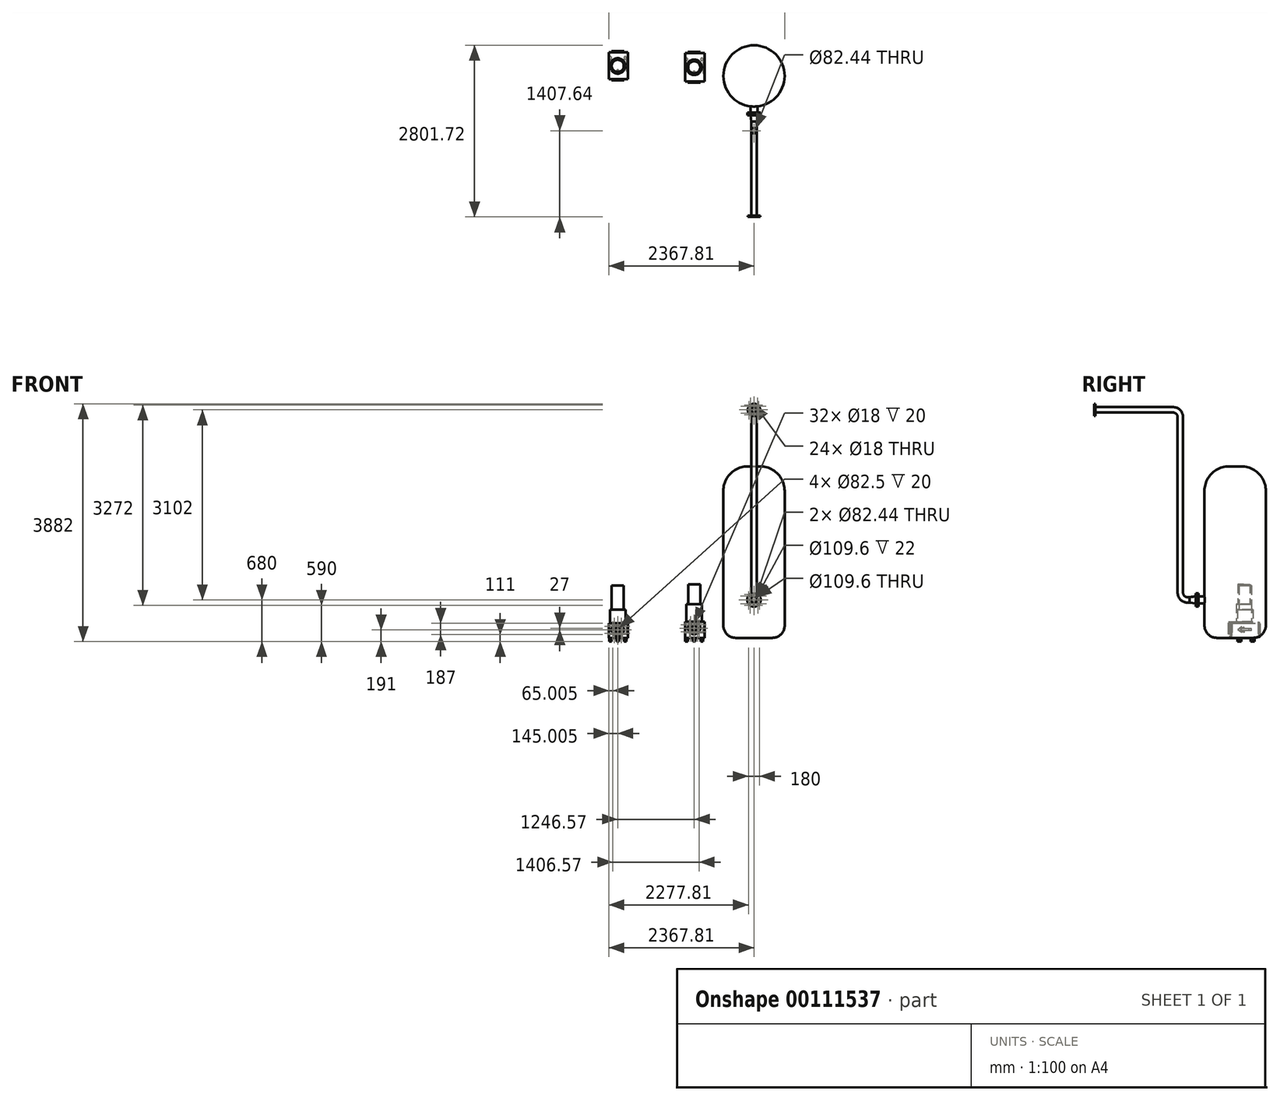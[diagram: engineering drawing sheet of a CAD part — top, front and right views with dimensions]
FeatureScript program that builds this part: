
annotation { "Feature Type Name" : "Feature", "Feature Type Description" : "" }
export const myFeature = defineFeature(function(context is Context, id is Id, definition is map)
    precondition{}
    {
        {
            var Q0;
            Q0=qCreatedBy(makeId("Top.planeOp"),FACE);
            var sketch = newSketch(context, id + "F0", { "sketchPlane" : qUnion([Q0])});
            skLineSegment(sketch, "E0.bottom", {"start": v(-836.3, 113.91) * mm, "end": v(-523.3, 113.91) * mm});
            skLineSegment(sketch, "E0.top", {"start": v(-836.3, -361.09) * mm, "end": v(-523.3, -361.09) * mm});
            skLineSegment(sketch, "E0.left", {"start": v(-836.3, 113.91) * mm, "end": v(-836.3, -361.09) * mm});
            skLineSegment(sketch, "E0.right", {"start": v(-523.3, 113.91) * mm, "end": v(-523.3, -361.09) * mm});
            skLineSegment(sketch, "E1.bottom", {"start": v(405.26, 101.65) * mm, "end": v(725.26, 101.65) * mm});
            skLineSegment(sketch, "E1.top", {"start": v(405.26, -398.35) * mm, "end": v(725.26, -398.35) * mm});
            skLineSegment(sketch, "E1.left", {"start": v(405.26, 101.65) * mm, "end": v(405.26, -398.35) * mm});
            skLineSegment(sketch, "E1.right", {"start": v(725.26, 101.65) * mm, "end": v(725.26, -398.35) * mm});
            skSolve(sketch);
        }
        {
            var Q0;
            Q0=makeQuery(id+"F0.imprint","IMPRINT",FACE,{"disambiguationData":[TD([[makeQuery(id+"F0.imprint","IMPRINT",EDGE,{"derivedFrom":sQuery(id+"F0.wireOp",EDGE,"E0.bottom")}),-1.0]])]});
            extrude(context, id + "F1", {"entities" : qUnion([Q0]), "depth" : 853 * mm});
        }
        {
            var Q0;
            Q0=makeQuery(id+"F1.opExtrude","SWEPT_FACE",FACE,{"disambiguationData":[OSD([sQuery(id+"F0.wireOp",EDGE,"E0.right")])]});
            cPlane(context, id + "F2", {"entities" : qUnion([Q0]), "cplaneType" : CPlaneType.OFFSET, "offset" : 168 * mm, "oppositeDirection" : true, "width" : 150 * mm, "height" : 150 * mm});
        }
        {
            var Q0;
            Q0=qCreatedBy(id+"F2.planeOp",FACE);
            var sketch = newSketch(context, id + "F3", { "sketchPlane" : qUnion([Q0])});
            skPoint(sketch, "E2", {"position": v(113.91, 426.5) * mm});
            skLineSegment(sketch, "E3", {"start": v(-27.09, 853) * mm, "end": v(-27.09, 463) * mm});
            skLineSegment(sketch, "E4", {"start": v(-27.09, 463) * mm, "end": v(-1.09, 463) * mm});
            skLineSegment(sketch, "E5", {"start": v(-1.09, 463) * mm, "end": v(-1.09, 236.83) * mm});
            skLineSegment(sketch, "E6", {"start": v(-1.09, 236.83) * mm, "end": v(113.91, 236.83) * mm});
            skLineSegment(sketch, "E7", {"start": v(-126.09, 872.7) * mm, "end": v(-126.09, -37.26) * mm, "construction": true});
            skLineSegment(sketch, "E8", {"start": v(-496.13, 131) * mm, "end": v(240.4, 131) * mm, "construction": true});
            skLineSegment(sketch, "E9", {"start": v(-27.09, 853) * mm, "end": v(558.03, 853) * mm});
            skLineSegment(sketch, "E10", {"start": v(558.03, 853) * mm, "end": v(558.03, 236.83) * mm});
            skLineSegment(sketch, "E11", {"start": v(558.03, 236.83) * mm, "end": v(113.91, 236.83) * mm});
            skSolve(sketch);
        }
        {
            var Q0;
            {var subQ2=sQuery(id+"F3.wireOp",EDGE,"E3");Q0=makeQuery(id+"F3.imprint","IMPRINT",FACE,{"disambiguationData":[TD([[makeQuery(id+"F3.imprint","IMPRINT",EDGE,{"derivedFrom":subQ2}),1.0]])]});}
            var Q1;
            Q1=sQuery(id+"F3.wireOp",EDGE,"E7");
            revolve(context, id + "F4", {"operationType" : NewBodyOperationType.REMOVE, "entities" : qUnion([Q0]), "axis" : qUnion([Q1]), "revolveType" : RevolveType.FULL, "oppositeDirection" : true});
        }
        {
            var Q0;
            Q0=makeQuery(id+"F1.opExtrude","SWEPT_FACE",FACE,{"disambiguationData":[OSD([sQuery(id+"F0.wireOp",EDGE,"E0.top")])]});
            var sketch = newSketch(context, id + "F5", { "sketchPlane" : qUnion([Q0])});
            skPoint(sketch, "E12.0", {"position": v(-691.3, 131) * mm});
            skCircle(sketch, "E13.2.0", {"center": v(-611.3, 131) * mm, "radius": 9 * mm});
            skCircle(sketch, "E13.1.0", {"center": v(-634.74, 74.43) * mm, "radius": 9 * mm});
            skCircle(sketch, "E14", {"center": v(-691.3, 131) * mm, "radius": 100 * mm});
            skCircle(sketch, "E13.3.0", {"center": v(-634.74, 187.57) * mm, "radius": 9 * mm});
            skCircle(sketch, "E15", {"center": v(-691.3, 51) * mm, "radius": 9 * mm});
            skCircle(sketch, "E16", {"center": v(-691.3, 131) * mm, "radius": 80 * mm, "construction": true});
            skCircle(sketch, "E17", {"center": v(-691.3, 131) * mm, "radius": 45.25 * mm});
            skCircle(sketch, "E13.6.0", {"center": v(-771.3, 131) * mm, "radius": 9 * mm});
            skCircle(sketch, "E18", {"center": v(-691.3, 131) * mm, "radius": 44.45 * mm});
            skCircle(sketch, "E13.4.0", {"center": v(-691.3, 211) * mm, "radius": 9 * mm});
            skCircle(sketch, "E13.7.0", {"center": v(-747.87, 74.43) * mm, "radius": 9 * mm});
            skCircle(sketch, "E13.5.0", {"center": v(-747.87, 187.57) * mm, "radius": 9 * mm});
            skCircle(sketch, "E19.0", {"center": v(-691.3, 131) * mm, "radius": 41.25 * mm});
            skSolve(sketch);
        }
        {
            var Q0;
            Q0=makeQuery(id+"F5.imprint","IMPRINT",FACE,{"disambiguationData":[TD([[makeQuery(id+"F5.imprint","IMPRINT",EDGE,{"derivedFrom":sQuery(id+"F5.wireOp",EDGE,"E14")}),-1.0]])]});
            var Q1;
            Q1=makeQuery(id+"F5.imprint","IMPRINT",FACE,{"disambiguationData":[TD([[makeQuery(id+"F5.imprint","IMPRINT",EDGE,{"derivedFrom":sQuery(id+"F5.wireOp",EDGE,"E13.5.0")}),1.0]])]});
            var Q2;
            Q2=makeQuery(id+"F5.imprint","IMPRINT",FACE,{"disambiguationData":[TD([[makeQuery(id+"F5.imprint","IMPRINT",EDGE,{"derivedFrom":sQuery(id+"F5.wireOp",EDGE,"E13.4.0")}),1.0]])]});
            var Q3;
            Q3=makeQuery(id+"F5.imprint","IMPRINT",FACE,{"disambiguationData":[TD([[makeQuery(id+"F5.imprint","IMPRINT",EDGE,{"derivedFrom":sQuery(id+"F5.wireOp",EDGE,"E13.3.0")}),1.0]])]});
            var Q4;
            Q4=makeQuery(id+"F5.imprint","IMPRINT",FACE,{"disambiguationData":[TD([[makeQuery(id+"F5.imprint","IMPRINT",EDGE,{"derivedFrom":sQuery(id+"F5.wireOp",EDGE,"E13.2.0")}),1.0]])]});
            var Q5;
            Q5=makeQuery(id+"F5.imprint","IMPRINT",FACE,{"disambiguationData":[TD([[makeQuery(id+"F5.imprint","IMPRINT",EDGE,{"derivedFrom":sQuery(id+"F5.wireOp",EDGE,"E13.1.0")}),1.0]])]});
            var Q6;
            Q6=makeQuery(id+"F5.imprint","IMPRINT",FACE,{"disambiguationData":[TD([[makeQuery(id+"F5.imprint","IMPRINT",EDGE,{"derivedFrom":sQuery(id+"F5.wireOp",EDGE,"E15")}),1.0]])]});
            var Q7;
            Q7=makeQuery(id+"F5.imprint","IMPRINT",FACE,{"disambiguationData":[TD([[makeQuery(id+"F5.imprint","IMPRINT",EDGE,{"derivedFrom":sQuery(id+"F5.wireOp",EDGE,"E13.7.0")}),1.0]])]});
            var Q8;
            Q8=makeQuery(id+"F5.imprint","IMPRINT",FACE,{"disambiguationData":[TD([[makeQuery(id+"F5.imprint","IMPRINT",EDGE,{"derivedFrom":sQuery(id+"F5.wireOp",EDGE,"E13.6.0")}),1.0]])]});
            var Q9;
            Q9=makeQuery(id+"F5.imprint","IMPRINT",FACE,{"disambiguationData":[TD([[makeQuery(id+"F5.imprint","IMPRINT",EDGE,{"derivedFrom":sQuery(id+"F5.wireOp",EDGE,"E19.0")}),1.0]])]});
            extrude(context, id + "F6", {"entities" : qUnion([Q0, Q1, Q2, Q3, Q4, Q5, Q6, Q7, Q8, Q9]), "operationType" : NewBodyOperationType.REMOVE, "oppositeDirection" : true, "depth" : 20 * mm});
        }
        {
            var Q0;
            Q0=makeQuery(id+"F1.opExtrude","SWEPT_FACE",FACE,{"disambiguationData":[OSD([sQuery(id+"F0.wireOp",EDGE,"E0.bottom")])]});
            var sketch = newSketch(context, id + "F7", { "sketchPlane" : qUnion([Q0])});
            skPoint(sketch, "E20.0", {"position": v(691.3, 131) * mm});
            skCircle(sketch, "E21.2.0", {"center": v(771.3, 131) * mm, "radius": 9 * mm});
            skCircle(sketch, "E21.1.0", {"center": v(747.87, 74.43) * mm, "radius": 9 * mm});
            skCircle(sketch, "E22", {"center": v(691.3, 131) * mm, "radius": 100 * mm});
            skCircle(sketch, "E21.3.0", {"center": v(747.87, 187.57) * mm, "radius": 9 * mm});
            skCircle(sketch, "E23", {"center": v(691.3, 51) * mm, "radius": 9 * mm});
            skCircle(sketch, "E24", {"center": v(691.3, 131) * mm, "radius": 80 * mm, "construction": true});
            skCircle(sketch, "E25", {"center": v(691.3, 131) * mm, "radius": 45.25 * mm});
            skCircle(sketch, "E21.6.0", {"center": v(611.3, 131) * mm, "radius": 9 * mm});
            skCircle(sketch, "E26", {"center": v(691.3, 131) * mm, "radius": 44.45 * mm});
            skCircle(sketch, "E21.4.0", {"center": v(691.3, 211) * mm, "radius": 9 * mm});
            skCircle(sketch, "E21.7.0", {"center": v(634.74, 74.43) * mm, "radius": 9 * mm});
            skCircle(sketch, "E21.5.0", {"center": v(634.74, 187.57) * mm, "radius": 9 * mm});
            skCircle(sketch, "E27.0", {"center": v(691.3, 131) * mm, "radius": 41.25 * mm});
            skSolve(sketch);
        }
        {
            var Q0;
            Q0=makeQuery(id+"F7.imprint","IMPRINT",FACE,{"disambiguationData":[TD([[makeQuery(id+"F7.imprint","IMPRINT",EDGE,{"derivedFrom":sQuery(id+"F7.wireOp",EDGE,"E22")}),-1.0]])]});
            var Q1;
            Q1=makeQuery(id+"F7.imprint","IMPRINT",FACE,{"disambiguationData":[TD([[makeQuery(id+"F7.imprint","IMPRINT",EDGE,{"derivedFrom":sQuery(id+"F7.wireOp",EDGE,"E21.4.0")}),1.0]])]});
            var Q2;
            Q2=makeQuery(id+"F7.imprint","IMPRINT",FACE,{"disambiguationData":[TD([[makeQuery(id+"F7.imprint","IMPRINT",EDGE,{"derivedFrom":sQuery(id+"F7.wireOp",EDGE,"E21.3.0")}),1.0]])]});
            var Q3;
            Q3=makeQuery(id+"F7.imprint","IMPRINT",FACE,{"disambiguationData":[TD([[makeQuery(id+"F7.imprint","IMPRINT",EDGE,{"derivedFrom":sQuery(id+"F7.wireOp",EDGE,"E21.5.0")}),1.0]])]});
            var Q4;
            Q4=makeQuery(id+"F7.imprint","IMPRINT",FACE,{"disambiguationData":[TD([[makeQuery(id+"F7.imprint","IMPRINT",EDGE,{"derivedFrom":sQuery(id+"F7.wireOp",EDGE,"E21.6.0")}),1.0]])]});
            var Q5;
            Q5=makeQuery(id+"F7.imprint","IMPRINT",FACE,{"disambiguationData":[TD([[makeQuery(id+"F7.imprint","IMPRINT",EDGE,{"derivedFrom":sQuery(id+"F7.wireOp",EDGE,"E21.7.0")}),1.0]])]});
            var Q6;
            Q6=makeQuery(id+"F7.imprint","IMPRINT",FACE,{"disambiguationData":[TD([[makeQuery(id+"F7.imprint","IMPRINT",EDGE,{"derivedFrom":sQuery(id+"F7.wireOp",EDGE,"E23")}),1.0]])]});
            var Q7;
            Q7=makeQuery(id+"F7.imprint","IMPRINT",FACE,{"disambiguationData":[TD([[makeQuery(id+"F7.imprint","IMPRINT",EDGE,{"derivedFrom":sQuery(id+"F7.wireOp",EDGE,"E21.1.0")}),1.0]])]});
            var Q8;
            Q8=makeQuery(id+"F7.imprint","IMPRINT",FACE,{"disambiguationData":[TD([[makeQuery(id+"F7.imprint","IMPRINT",EDGE,{"derivedFrom":sQuery(id+"F7.wireOp",EDGE,"E21.2.0")}),1.0]])]});
            var Q9;
            Q9=makeQuery(id+"F7.imprint","IMPRINT",FACE,{"disambiguationData":[TD([[makeQuery(id+"F7.imprint","IMPRINT",EDGE,{"derivedFrom":sQuery(id+"F7.wireOp",EDGE,"E27.0")}),1.0]])]});
            extrude(context, id + "F8", {"entities" : qUnion([Q0, Q1, Q2, Q3, Q4, Q5, Q6, Q7, Q8, Q9]), "operationType" : NewBodyOperationType.REMOVE, "oppositeDirection" : true, "depth" : 20 * mm});
        }
        {
            var Q0;
            Q0=makeQuery(id+"F1.opExtrude","SWEPT_FACE",FACE,{"disambiguationData":[OSD([sQuery(id+"F0.wireOp",EDGE,"E0.right")])]});
            var sketch = newSketch(context, id + "F9", { "sketchPlane" : qUnion([Q0])});
            skLineSegment(sketch, "E28", {"start": v(-26.3, 131) * mm, "end": v(-26.3, 146.57) * mm});
            skLineSegment(sketch, "E29", {"start": v(-26.3, 146.57) * mm, "end": v(-146.38, 146.57) * mm});
            skLineSegment(sketch, "E30", {"start": v(-146.38, 146.57) * mm, "end": v(-146.38, 177.7) * mm});
            skLineSegment(sketch, "E31", {"start": v(-146.38, 177.7) * mm, "end": v(-207.53, 131) * mm});
            skLineSegment(sketch, "E32.0", {"start": v(-496.13, 131) * mm, "end": v(240.4, 131) * mm});
            skLineSegment(sketch, "E33.MirrorCS", {"start": v(-26.3, 131) * mm, "end": v(-26.3, 115.43) * mm});
            skLineSegment(sketch, "E34.MirrorCS", {"start": v(-26.3, 115.43) * mm, "end": v(-146.38, 115.43) * mm});
            skLineSegment(sketch, "E35.MirrorCS", {"start": v(-146.38, 115.43) * mm, "end": v(-146.38, 84.3) * mm});
            skLineSegment(sketch, "E36.MirrorCS", {"start": v(-146.38, 84.3) * mm, "end": v(-207.53, 131) * mm});
            skSolve(sketch);
        }
        {
            var Q0;
            Q0=qSketchRegion(id+"F9",true);
            extrude(context, id + "F10", {"entities" : qUnion([Q0]), "operationType" : NewBodyOperationType.REMOVE, "oppositeDirection" : true, "depth" : 25 * mm});
        }
        {
            var Q0;
            Q0=makeQuery(id+"F0.imprint","IMPRINT",FACE,{"disambiguationData":[TD([[makeQuery(id+"F0.imprint","IMPRINT",EDGE,{"derivedFrom":sQuery(id+"F0.wireOp",EDGE,"E1.bottom")}),-1.0]])]});
            extrude(context, id + "F11", {"entities" : qUnion([Q0]), "depth" : (736 + 140) * mm});
        }
        {
            var Q0;
            Q0=makeQuery(id+"F11.opExtrude","SWEPT_FACE",FACE,{"disambiguationData":[OSD([sQuery(id+"F0.wireOp",EDGE,"E1.right")])]});
            cPlane(context, id + "F12", {"entities" : qUnion([Q0]), "cplaneType" : CPlaneType.OFFSET, "offset" : 170 * mm, "oppositeDirection" : true, "width" : 150 * mm, "height" : 150 * mm});
        }
        {
            var Q0;
            Q0=qCreatedBy(id+"F12.planeOp",FACE);
            var sketch = newSketch(context, id + "F13", { "sketchPlane" : qUnion([Q0])});
            skLineSegment(sketch, "E37", {"start": v(-148.35, 1099.62) * mm, "end": v(-148.35, -337.67) * mm, "construction": true});
            skLineSegment(sketch, "E38", {"start": v(-1098.71, 158) * mm, "end": v(911.34, 158) * mm, "construction": true});
            skLineSegment(sketch, "E39", {"start": v(-49.35, 894.2) * mm, "end": v(-49.35, 551.68) * mm});
            skLineSegment(sketch, "E40", {"start": v(-49.35, 551.68) * mm, "end": v(-23.35, 551.68) * mm});
            skLineSegment(sketch, "E41", {"start": v(-23.35, 551.68) * mm, "end": v(-23.35, 262.71) * mm});
            skLineSegment(sketch, "E42", {"start": v(-23.35, 262.71) * mm, "end": v(461.98, 262.71) * mm});
            skLineSegment(sketch, "E43", {"start": v(461.98, 262.71) * mm, "end": v(461.98, 894.2) * mm});
            skLineSegment(sketch, "E44", {"start": v(461.98, 894.2) * mm, "end": v(-49.35, 894.2) * mm});
            skSolve(sketch);
        }
        {
            var Q0;
            Q0=qSketchRegion(id+"F13",true);
            var Q1;
            Q1=sQuery(id+"F13.wireOp",EDGE,"E37");
            revolve(context, id + "F14", {"operationType" : NewBodyOperationType.REMOVE, "entities" : qUnion([Q0]), "axis" : qUnion([Q1]), "revolveType" : RevolveType.FULL, "oppositeDirection" : true});
        }
        {
            var Q0;
            Q0=makeQuery(id+"F11.opExtrude","SWEPT_FACE",FACE,{"disambiguationData":[OSD([sQuery(id+"F0.wireOp",EDGE,"E1.top")])]});
            var sketch = newSketch(context, id + "F15", { "sketchPlane" : qUnion([Q0])});
            skPoint(sketch, "E45.0", {"position": v(555.26, 158) * mm});
            skCircle(sketch, "E46.2.0", {"center": v(635.26, 158) * mm, "radius": 9 * mm});
            skCircle(sketch, "E46.1.0", {"center": v(611.83, 101.43) * mm, "radius": 9 * mm});
            skCircle(sketch, "E47", {"center": v(555.26, 158) * mm, "radius": 100 * mm});
            skCircle(sketch, "E46.3.0", {"center": v(611.83, 214.57) * mm, "radius": 9 * mm});
            skCircle(sketch, "E48", {"center": v(555.26, 78) * mm, "radius": 9 * mm});
            skCircle(sketch, "E49", {"center": v(555.26, 158) * mm, "radius": 80 * mm, "construction": true});
            skCircle(sketch, "E50", {"center": v(555.26, 158) * mm, "radius": 45.25 * mm});
            skCircle(sketch, "E46.6.0", {"center": v(475.26, 158) * mm, "radius": 9 * mm});
            skCircle(sketch, "E51", {"center": v(555.26, 158) * mm, "radius": 44.45 * mm});
            skCircle(sketch, "E46.4.0", {"center": v(555.26, 238) * mm, "radius": 9 * mm});
            skCircle(sketch, "E46.7.0", {"center": v(498.7, 101.43) * mm, "radius": 9 * mm});
            skCircle(sketch, "E46.5.0", {"center": v(498.7, 214.57) * mm, "radius": 9 * mm});
            skCircle(sketch, "E52.0", {"center": v(555.26, 158) * mm, "radius": 41.25 * mm});
            skSolve(sketch);
        }
        {
            var Q0;
            Q0=makeQuery(id+"F15.imprint","IMPRINT",FACE,{"disambiguationData":[TD([[makeQuery(id+"F15.imprint","IMPRINT",EDGE,{"derivedFrom":sQuery(id+"F15.wireOp",EDGE,"E47")}),-1.0]])]});
            var Q1;
            Q1=makeQuery(id+"F15.imprint","IMPRINT",FACE,{"disambiguationData":[TD([[makeQuery(id+"F15.imprint","IMPRINT",EDGE,{"derivedFrom":sQuery(id+"F15.wireOp",EDGE,"E46.5.0")}),1.0]])]});
            var Q2;
            Q2=makeQuery(id+"F15.imprint","IMPRINT",FACE,{"disambiguationData":[TD([[makeQuery(id+"F15.imprint","IMPRINT",EDGE,{"derivedFrom":sQuery(id+"F15.wireOp",EDGE,"E46.4.0")}),1.0]])]});
            var Q3;
            Q3=makeQuery(id+"F15.imprint","IMPRINT",FACE,{"disambiguationData":[TD([[makeQuery(id+"F15.imprint","IMPRINT",EDGE,{"derivedFrom":sQuery(id+"F15.wireOp",EDGE,"E46.3.0")}),1.0]])]});
            var Q4;
            Q4=makeQuery(id+"F15.imprint","IMPRINT",FACE,{"disambiguationData":[TD([[makeQuery(id+"F15.imprint","IMPRINT",EDGE,{"derivedFrom":sQuery(id+"F15.wireOp",EDGE,"E46.2.0")}),1.0]])]});
            var Q5;
            Q5=makeQuery(id+"F15.imprint","IMPRINT",FACE,{"disambiguationData":[TD([[makeQuery(id+"F15.imprint","IMPRINT",EDGE,{"derivedFrom":sQuery(id+"F15.wireOp",EDGE,"E52.0")}),1.0]])]});
            var Q6;
            Q6=makeQuery(id+"F15.imprint","IMPRINT",FACE,{"disambiguationData":[TD([[makeQuery(id+"F15.imprint","IMPRINT",EDGE,{"derivedFrom":sQuery(id+"F15.wireOp",EDGE,"E46.1.0")}),1.0]])]});
            var Q7;
            Q7=makeQuery(id+"F15.imprint","IMPRINT",FACE,{"disambiguationData":[TD([[makeQuery(id+"F15.imprint","IMPRINT",EDGE,{"derivedFrom":sQuery(id+"F15.wireOp",EDGE,"E48")}),1.0]])]});
            var Q8;
            Q8=makeQuery(id+"F15.imprint","IMPRINT",FACE,{"disambiguationData":[TD([[makeQuery(id+"F15.imprint","IMPRINT",EDGE,{"derivedFrom":sQuery(id+"F15.wireOp",EDGE,"E46.7.0")}),1.0]])]});
            var Q9;
            Q9=makeQuery(id+"F15.imprint","IMPRINT",FACE,{"disambiguationData":[TD([[makeQuery(id+"F15.imprint","IMPRINT",EDGE,{"derivedFrom":sQuery(id+"F15.wireOp",EDGE,"E46.6.0")}),1.0]])]});
            extrude(context, id + "F16", {"entities" : qUnion([Q0, Q1, Q2, Q3, Q4, Q5, Q6, Q7, Q8, Q9]), "operationType" : NewBodyOperationType.REMOVE, "oppositeDirection" : true, "depth" : 20 * mm});
        }
        {
            var Q0;
            Q0=makeQuery(id+"F11.opExtrude","SWEPT_FACE",FACE,{"disambiguationData":[OSD([sQuery(id+"F0.wireOp",EDGE,"E1.bottom")])]});
            var sketch = newSketch(context, id + "F17", { "sketchPlane" : qUnion([Q0])});
            skPoint(sketch, "E53.0", {"position": v(-555.26, 158) * mm});
            skCircle(sketch, "E54.2.0", {"center": v(-475.26, 158) * mm, "radius": 9 * mm});
            skCircle(sketch, "E54.1.0", {"center": v(-498.7, 101.43) * mm, "radius": 9 * mm});
            skCircle(sketch, "E55", {"center": v(-555.26, 158) * mm, "radius": 100 * mm});
            skCircle(sketch, "E54.3.0", {"center": v(-498.7, 214.57) * mm, "radius": 9 * mm});
            skCircle(sketch, "E56", {"center": v(-555.26, 78) * mm, "radius": 9 * mm});
            skCircle(sketch, "E57", {"center": v(-555.26, 158) * mm, "radius": 80 * mm, "construction": true});
            skCircle(sketch, "E58", {"center": v(-555.26, 158) * mm, "radius": 45.25 * mm});
            skCircle(sketch, "E54.6.0", {"center": v(-635.26, 158) * mm, "radius": 9 * mm});
            skCircle(sketch, "E59", {"center": v(-555.26, 158) * mm, "radius": 44.45 * mm});
            skCircle(sketch, "E54.4.0", {"center": v(-555.26, 238) * mm, "radius": 9 * mm});
            skCircle(sketch, "E54.7.0", {"center": v(-611.83, 101.43) * mm, "radius": 9 * mm});
            skCircle(sketch, "E54.5.0", {"center": v(-611.83, 214.57) * mm, "radius": 9 * mm});
            skCircle(sketch, "E60.0", {"center": v(-555.26, 158) * mm, "radius": 41.25 * mm});
            skSolve(sketch);
        }
        {
            var Q0;
            Q0=makeQuery(id+"F17.imprint","IMPRINT",FACE,{"disambiguationData":[TD([[makeQuery(id+"F17.imprint","IMPRINT",EDGE,{"derivedFrom":sQuery(id+"F17.wireOp",EDGE,"E55")}),-1.0]])]});
            var Q1;
            Q1=makeQuery(id+"F17.imprint","IMPRINT",FACE,{"disambiguationData":[TD([[makeQuery(id+"F17.imprint","IMPRINT",EDGE,{"derivedFrom":sQuery(id+"F17.wireOp",EDGE,"E54.4.0")}),1.0]])]});
            var Q2;
            Q2=makeQuery(id+"F17.imprint","IMPRINT",FACE,{"disambiguationData":[TD([[makeQuery(id+"F17.imprint","IMPRINT",EDGE,{"derivedFrom":sQuery(id+"F17.wireOp",EDGE,"E54.3.0")}),1.0]])]});
            var Q3;
            Q3=makeQuery(id+"F17.imprint","IMPRINT",FACE,{"disambiguationData":[TD([[makeQuery(id+"F17.imprint","IMPRINT",EDGE,{"derivedFrom":sQuery(id+"F17.wireOp",EDGE,"E54.1.0")}),1.0]])]});
            var Q4;
            Q4=makeQuery(id+"F17.imprint","IMPRINT",FACE,{"disambiguationData":[TD([[makeQuery(id+"F17.imprint","IMPRINT",EDGE,{"derivedFrom":sQuery(id+"F17.wireOp",EDGE,"E60.0")}),1.0]])]});
            var Q5;
            Q5=makeQuery(id+"F17.imprint","IMPRINT",FACE,{"disambiguationData":[TD([[makeQuery(id+"F17.imprint","IMPRINT",EDGE,{"derivedFrom":sQuery(id+"F17.wireOp",EDGE,"E54.5.0")}),1.0]])]});
            var Q6;
            Q6=makeQuery(id+"F17.imprint","IMPRINT",FACE,{"disambiguationData":[TD([[makeQuery(id+"F17.imprint","IMPRINT",EDGE,{"derivedFrom":sQuery(id+"F17.wireOp",EDGE,"E54.6.0")}),1.0]])]});
            var Q7;
            Q7=makeQuery(id+"F17.imprint","IMPRINT",FACE,{"disambiguationData":[TD([[makeQuery(id+"F17.imprint","IMPRINT",EDGE,{"derivedFrom":sQuery(id+"F17.wireOp",EDGE,"E54.7.0")}),1.0]])]});
            var Q8;
            Q8=makeQuery(id+"F17.imprint","IMPRINT",FACE,{"disambiguationData":[TD([[makeQuery(id+"F17.imprint","IMPRINT",EDGE,{"derivedFrom":sQuery(id+"F17.wireOp",EDGE,"E56")}),1.0]])]});
            var Q9;
            Q9=makeQuery(id+"F17.imprint","IMPRINT",FACE,{"disambiguationData":[TD([[makeQuery(id+"F17.imprint","IMPRINT",EDGE,{"derivedFrom":sQuery(id+"F17.wireOp",EDGE,"E54.2.0")}),1.0]])]});
            extrude(context, id + "F18", {"entities" : qUnion([Q0, Q1, Q2, Q3, Q4, Q5, Q6, Q7, Q8, Q9]), "operationType" : NewBodyOperationType.REMOVE, "oppositeDirection" : true, "depth" : 20 * mm});
        }
        {
            var Q0;
            Q0=makeQuery(id+"F11.opExtrude","SWEPT_FACE",FACE,{"disambiguationData":[OSD([sQuery(id+"F0.wireOp",EDGE,"E1.right")])]});
            var sketch = newSketch(context, id + "F19", { "sketchPlane" : qUnion([Q0])});
            skLineSegment(sketch, "E61", {"start": v(-63.56, 131.36) * mm, "end": v(-63.56, 146.92) * mm});
            skLineSegment(sketch, "E62", {"start": v(-63.56, 146.92) * mm, "end": v(-183.64, 146.92) * mm});
            skLineSegment(sketch, "E63", {"start": v(-183.64, 146.92) * mm, "end": v(-183.64, 178.05) * mm});
            skLineSegment(sketch, "E64", {"start": v(-183.64, 178.05) * mm, "end": v(-244.79, 131.36) * mm});
            skLineSegment(sketch, "E65.0", {"start": v(-533.38, 131.36) * mm, "end": v(203.14, 131.36) * mm});
            skLineSegment(sketch, "E66.MirrorCS", {"start": v(-63.56, 131.36) * mm, "end": v(-63.56, 115.8) * mm});
            skLineSegment(sketch, "E67.MirrorCS", {"start": v(-63.56, 115.8) * mm, "end": v(-183.64, 115.8) * mm});
            skLineSegment(sketch, "E68.MirrorCS", {"start": v(-183.64, 115.8) * mm, "end": v(-183.64, 84.66) * mm});
            skLineSegment(sketch, "E69.MirrorCS", {"start": v(-183.64, 84.66) * mm, "end": v(-244.79, 131.36) * mm});
            skSolve(sketch);
        }
        {
            var Q0;
            {var subQ2=sQuery(id+"F19.wireOp",EDGE,"E61");Q0=makeQuery(id+"F19.imprint","IMPRINT",FACE,{"disambiguationData":[TD([[makeQuery(id+"F19.imprint","IMPRINT",EDGE,{"derivedFrom":subQ2}),1.0]])]});}
            var Q1;
            {var subQ1=sQuery(id+"F19.wireOp",EDGE,"E66.MirrorCS");Q1=makeQuery(id+"F19.imprint","IMPRINT",FACE,{"disambiguationData":[TD([[makeQuery(id+"F19.imprint","IMPRINT",EDGE,{"derivedFrom":subQ1}),-1.0]])]});}
            var Q2;
            Q2=sQuery(id+"F19.wireOp",EDGE,"E61");
            var Q3;
            Q3=sQuery(id+"F19.wireOp",EDGE,"E62");
            var Q4;
            Q4=sQuery(id+"F19.wireOp",EDGE,"E63");
            var Q5;
            Q5=sQuery(id+"F19.wireOp",EDGE,"E64");
            var Q6;
            Q6=sQuery(id+"F19.wireOp",EDGE,"E65.0");
            var Q7;
            Q7=sQuery(id+"F19.wireOp",EDGE,"E66.MirrorCS");
            var Q8;
            Q8=sQuery(id+"F19.wireOp",EDGE,"E67.MirrorCS");
            var Q9;
            Q9=sQuery(id+"F19.wireOp",EDGE,"E68.MirrorCS");
            var Q10;
            Q10=sQuery(id+"F19.wireOp",EDGE,"E69.MirrorCS");
            extrude(context, id + "F20", {"entities" : qUnion([Q0, Q1]), "operationType" : NewBodyOperationType.REMOVE, "surfaceEntities" : qUnion([Q2, Q3, Q4, Q5, Q6, Q7, Q8, Q9, Q10]), "oppositeDirection" : true, "depth" : 25 * mm});
        }
        {
            var Q0;
            Q0=makeQuery(id+"F0.imprint","IMPRINT",FACE,{"disambiguationData":[TD([[makeQuery(id+"F0.imprint","IMPRINT",EDGE,{"derivedFrom":sQuery(id+"F0.wireOp",EDGE,"E1.bottom")}),-1.0]])]});
            var sketch = newSketch(context, id + "F21", { "sketchPlane" : qUnion([Q0])});
            skPoint(sketch, "E70.0", {"position": v(555.26, -148.35) * mm});
            skLineSegment(sketch, "E70.1", {"start": v(555.26, -1098.71) * mm, "end": v(555.26, 911.34) * mm});
            skCircle(sketch, "E71", {"center": v(555.26, -233.35) * mm, "radius": 20.21 * mm});
            skCircle(sketch, "E72", {"center": v(680.26, -18.35) * mm, "radius": 20.21 * mm});
            skCircle(sketch, "E73.MirrorC", {"center": v(430.26, -18.35) * mm, "radius": 20.21 * mm});
            skSolve(sketch);
        }
        {
            var Q0;
            Q0=qSketchRegion(id+"F21",true);
            extrude(context, id + "F22", {"entities" : qUnion([Q0]), "operationType" : NewBodyOperationType.ADD, "oppositeDirection" : true, "depth" : 60 * mm});
        }
        {
            var Q0;
            Q0=makeQuery(id+"F1.opExtrude","CAP_FACE",FACE,{"disambiguationData":[OSD([sQuery(id+"F0.wireOp",EDGE,"E0.bottom"),sQuery(id+"F0.wireOp",EDGE,"E0.top"),sQuery(id+"F0.wireOp",EDGE,"E0.left"),sQuery(id+"F0.wireOp",EDGE,"E0.right")])],"isStart":true});
            var sketch = newSketch(context, id + "F23", { "sketchPlane" : qUnion([Q0])});
            skPoint(sketch, "E74.0", {"position": v(-691.3, 126.09) * mm});
            skLineSegment(sketch, "E74.1", {"start": v(-691.3, -824.27) * mm, "end": v(-691.3, 1185.78) * mm});
            skCircle(sketch, "E75", {"center": v(-691.3, 211.09) * mm, "radius": 20.21 * mm});
            skCircle(sketch, "E76", {"center": v(-571.3, -3.91) * mm, "radius": 20.21 * mm});
            skCircle(sketch, "E77.MirrorC", {"center": v(-811.3, -3.91) * mm, "radius": 20.21 * mm});
            skLineSegment(sketch, "E78.0", {"start": v(-691.3, 496.13) * mm, "end": v(-691.3, -240.4) * mm});
            skSolve(sketch);
        }
        {
            var Q0;
            Q0=qSketchRegion(id+"F23",true);
            extrude(context, id + "F24", {"entities" : qUnion([Q0]), "operationType" : NewBodyOperationType.ADD, "depth" : 60 * mm});
        }
        {
            var Q0;
            Q0=qCreatedBy(makeId("Top.planeOp"),FACE);
            var sketch = newSketch(context, id + "F25", { "sketchPlane" : qUnion([Q0])});
            skCircle(sketch, "E79", {"center": v(1531.5, -290.09) * mm, "radius": 500 * mm});
            skLineSegment(sketch, "E80", {"start": v(1531.5, -290.09) * mm, "end": v(1531.5, -790.09) * mm, "construction": true});
            skSolve(sketch);
        }
        {
            var Q0;
            Q0=qSketchRegion(id+"F25",true);
            extrude(context, id + "F26", {"entities" : qUnion([Q0]), "depth" : 2800 * mm});
        }
        {
            var Q0;
            Q0=makeQuery(id+"F26.opExtrude","CAP_EDGE",EDGE,{"disambiguationData":[OSD([sQuery(id+"F25.wireOp",EDGE,"E79")])],"isStart":false});
            fillet(context, id + "F27", {"entities" : qUnion([Q0]), "radius" : 400 * mm, "tangentPropagation" : true, "allowEdgeOverflow" : false});
        }
        {
            var Q0;
            Q0=makeQuery(id+"F26.opExtrude","CAP_EDGE",EDGE,{"disambiguationData":[OSD([sQuery(id+"F25.wireOp",EDGE,"E79")])],"isStart":true});
            fillet(context, id + "F28", {"entities" : qUnion([Q0]), "radius" : 200 * mm, "tangentPropagation" : true, "allowEdgeOverflow" : false});
        }
        {
            var Q0;
            Q0=sQuery(id+"F25.wireOp",EDGE,"E80");
            var Q1;
            Q1=sQuery(id+"F25.wireOp",VERTEX,"E80.end");
            cPlane(context, id + "F29", {"entities" : qUnion([Q0, Q1]), "cplaneType" : CPlaneType.LINE_POINT, "offset" : 150 * mm, "width" : 150 * mm, "height" : 150 * mm});
        }
        {
            var Q0;
            Q0=qCreatedBy(id+"F29.planeOp",FACE);
            var sketch = newSketch(context, id + "F30", { "sketchPlane" : qUnion([Q0])});
            skPoint(sketch, "E81.0", {"position": v(1531.5, 0) * mm});
            skCircle(sketch, "E82", {"center": v(1531.5, 620) * mm, "radius": 58 * mm});
            skCircle(sketch, "E83.0", {"center": v(1531.5, 620) * mm, "radius": 54.8 * mm});
            skSolve(sketch);
        }
        {
            var Q0;
            Q0=qSketchRegion(id+"F30",true);
            extrude(context, id + "F31", {"entities" : qUnion([Q0]), "operationType" : NewBodyOperationType.ADD, "depth" : 98 * mm, "hasSecondDirection" : true, "secondDirectionOppositeDirection" : true, "secondDirectionDepth" : 20 * mm});
        }
        {
            var Q0;
            Q0=makeQuery(id+"F31.opExtrude","CAP_FACE",FACE,{"disambiguationData":[OSD([sQuery(id+"F30.wireOp",EDGE,"E82"),sQuery(id+"F30.wireOp",EDGE,"E83.0")])],"isStart":false});
            var sketch = newSketch(context, id + "F32", { "sketchPlane" : qUnion([Q0])});
            skCircle(sketch, "E84", {"center": v(1531.5, 620) * mm, "radius": 90 * mm, "construction": true});
            skCircle(sketch, "E85", {"center": v(1531.5, 620) * mm, "radius": 110 * mm});
            skCircle(sketch, "E86", {"center": v(1531.5, 620) * mm, "radius": 57.15 * mm});
            skCircle(sketch, "E87", {"center": v(1531.5, 620) * mm, "radius": 58 * mm});
            skCircle(sketch, "E88.1.0", {"center": v(1595.14, 556.36) * mm, "radius": 9 * mm});
            skCircle(sketch, "E88.2.0", {"center": v(1621.5, 620) * mm, "radius": 9 * mm});
            skCircle(sketch, "E88.4.0", {"center": v(1531.5, 710) * mm, "radius": 9 * mm});
            skCircle(sketch, "E88.6.0", {"center": v(1441.5, 620) * mm, "radius": 9 * mm});
            skCircle(sketch, "E88.7.0", {"center": v(1467.86, 556.36) * mm, "radius": 9 * mm});
            skCircle(sketch, "E89", {"center": v(1531.5, 530) * mm, "radius": 9 * mm});
            skCircle(sketch, "E88.3.0", {"center": v(1595.14, 683.64) * mm, "radius": 9 * mm});
            skCircle(sketch, "E88.5.0", {"center": v(1467.86, 683.64) * mm, "radius": 9 * mm});
            skCircle(sketch, "E90.0", {"center": v(1531.5, 620) * mm, "radius": 54.8 * mm});
            skSolve(sketch);
        }
        {
            var Q0;
            Q0=qSketchRegion(id+"F32",true);
            var Q1;
            Q1=makeQuery(id+"F32.imprint","IMPRINT",FACE,{"disambiguationData":[TD([[makeQuery(id+"F32.imprint","IMPRINT",EDGE,{"derivedFrom":sQuery(id+"F32.wireOp",EDGE,"E86")}),-1.0]])]});
            var Q2;
            Q2=makeQuery(id+"F32.imprint","IMPRINT",FACE,{"disambiguationData":[TD([[makeQuery(id+"F32.imprint","IMPRINT",EDGE,{"derivedFrom":sQuery(id+"F32.wireOp",EDGE,"E86")}),1.0]])]});
            extrude(context, id + "F33", {"entities" : qUnion([Q0, Q1, Q2]), "operationType" : NewBodyOperationType.ADD, "depth" : 22 * mm});
        }
        {
            var Q0;
            Q0=makeQuery(id+"F33.opExtrude","CAP_FACE",FACE,{"disambiguationData":[OSD([sQuery(id+"F32.wireOp",EDGE,"E85"),sQuery(id+"F32.wireOp",EDGE,"E88.1.0"),sQuery(id+"F32.wireOp",EDGE,"E88.2.0"),sQuery(id+"F32.wireOp",EDGE,"E88.4.0"),sQuery(id+"F32.wireOp",EDGE,"E88.6.0"),sQuery(id+"F32.wireOp",EDGE,"E88.7.0"),sQuery(id+"F32.wireOp",EDGE,"E89"),sQuery(id+"F32.wireOp",EDGE,"E88.3.0"),sQuery(id+"F32.wireOp",EDGE,"E88.5.0"),sQuery(id+"F32.wireOp",EDGE,"E90.0")])],"isStart":false});
            extrude(context, id + "F34", {"entities" : qUnion([Q0]), "depth" : 22 * mm});
        }
        {
            var Q0;
            Q0=sQuery(id+"F30.wireOp",VERTEX,"E83.0.center");
            var Q1;
            Q1=qCreatedBy(makeId("Right.planeOp"),FACE);
            cPlane(context, id + "F35", {"entities" : qUnion([Q0, Q1]), "cplaneType" : CPlaneType.PLANE_POINT, "offset" : 150 * mm, "width" : 150 * mm, "height" : 150 * mm});
        }
        {
            var Q0;
            Q0=qCreatedBy(id+"F35.planeOp",FACE);
            var sketch = newSketch(context, id + "F36", { "sketchPlane" : qUnion([Q0])});
            skLineSegment(sketch, "E91.0", {"start": v(-932.09, 510) * mm, "end": v(-932.09, 730) * mm});
            skPoint(sketch, "E92", {"position": v(-932.09, 620) * mm});
            skLineSegment(sketch, "E93", {"start": v(-932.09, 620) * mm, "end": v(-1068.17, 620) * mm, "construction": true});
            skLineSegment(sketch, "E94", {"start": v(-1184.17, 736) * mm, "end": v(-1184.17, 3606) * mm});
            skPoint(sketch, "E95.visualSharp", {"position": v(-1184.17, 620) * mm});
            skArc(sketch, "E95.filletArc", {"start": v(-1184.17, 736) * mm, "mid": v(-1150.2, 653.98) * mm, "end": v(-1068.17, 620) * mm});
            skLineSegment(sketch, "E96", {"start": v(-1300.17, 3722) * mm, "end": v(-1315.41, 3722) * mm});
            skPoint(sketch, "E97.visualSharp", {"position": v(-1184.17, 3722) * mm});
            skArc(sketch, "E97.filletArc", {"start": v(-1184.17, 3606) * mm, "mid": v(-1218.15, 3688.02) * mm, "end": v(-1300.17, 3722) * mm});
            skSolve(sketch);
        }
        {
            var Q0;
            Q0=sQuery(id+"F36.wireOp",EDGE,"E93");
            var Q1;
            Q1=sQuery(id+"F36.wireOp",VERTEX,"E95.visualSharp");
            cPlane(context, id + "F37", {"entities" : qUnion([Q0, Q1]), "cplaneType" : CPlaneType.LINE_POINT, "offset" : 150 * mm, "width" : 150 * mm, "height" : 150 * mm});
        }
        {
            var Q0;
            Q0=sQuery(id+"F36.wireOp",EDGE,"E94");
            var Q1;
            Q1=sQuery(id+"F36.wireOp",VERTEX,"E97.visualSharp");
            cPlane(context, id + "F38", {"entities" : qUnion([Q0, Q1]), "cplaneType" : CPlaneType.LINE_POINT, "offset" : 150 * mm, "width" : 150 * mm, "height" : 150 * mm});
        }
        {
            var Q0;
            Q0=qCreatedBy(id+"F38.planeOp",FACE);
            var sketch = newSketch(context, id + "F39", { "sketchPlane" : qUnion([Q0])});
            skPoint(sketch, "E98.0", {"position": v(4560.27, -1973.37) * mm});
            skLineSegment(sketch, "E99", {"start": v(1611.5, -2671.8) * mm, "end": v(5151.5, -2671.8) * mm});
            skLineSegment(sketch, "E100", {"start": v(5231.5, -1954.56) * mm, "end": v(5231.5, -2751.8) * mm});
            skPoint(sketch, "E101.visualSharp", {"position": v(5231.5, -2671.8) * mm});
            skArc(sketch, "E101.filletArc", {"start": v(5231.5, -2751.8) * mm, "mid": v(5208.06, -2695.24) * mm, "end": v(5151.5, -2671.8) * mm});
            skPoint(sketch, "E102.0", {"position": v(1531.5, -1315.41) * mm});
            skLineSegment(sketch, "E103", {"start": v(1531.5, -1315.41) * mm, "end": v(1531.5, -2591.8) * mm});
            skPoint(sketch, "E104.visualSharp", {"position": v(1531.5, -2671.8) * mm});
            skArc(sketch, "E104.filletArc", {"start": v(1531.5, -2591.8) * mm, "mid": v(1554.93, -2648.38) * mm, "end": v(1611.5, -2671.8) * mm});
            skSolve(sketch);
        }
        {
            var Q0;
            Q0=makeQuery(id+"F34.opExtrude","CAP_FACE",FACE,{"disambiguationData":[OSD([sQuery(id+"F32.wireOp",EDGE,"E85"),sQuery(id+"F32.wireOp",EDGE,"E88.1.0"),sQuery(id+"F32.wireOp",EDGE,"E88.2.0"),sQuery(id+"F32.wireOp",EDGE,"E88.4.0"),sQuery(id+"F32.wireOp",EDGE,"E88.6.0"),sQuery(id+"F32.wireOp",EDGE,"E88.7.0"),sQuery(id+"F32.wireOp",EDGE,"E89"),sQuery(id+"F32.wireOp",EDGE,"E88.3.0"),sQuery(id+"F32.wireOp",EDGE,"E88.5.0"),sQuery(id+"F32.wireOp",EDGE,"E90.0")])],"isStart":false});
            var sketch = newSketch(context, id + "F40", { "sketchPlane" : qUnion([Q0])});
            skCircle(sketch, "E105.0", {"center": v(1531.5, 620) * mm, "radius": 54.8 * mm});
            skCircle(sketch, "E105.1", {"center": v(1531.5, 620) * mm, "radius": 58 * mm});
            skSolve(sketch);
        }
        {
            var Q0;
            Q0=qCreatedBy(id+"F35.planeOp",FACE);
            var sketch = newSketch(context, id + "F41", { "sketchPlane" : qUnion([Q0])});
            skLineSegment(sketch, "E106.0", {"start": v(-932.09, 562) * mm, "end": v(-932.09, 678) * mm});
            skLineSegment(sketch, "E106.1", {"start": v(-932.09, 565.2) * mm, "end": v(-932.09, 674.8) * mm});
            skLineSegment(sketch, "E107", {"start": v(-932.09, 678) * mm, "end": v(-1032.09, 664.45) * mm});
            skLineSegment(sketch, "E108.0", {"start": v(-932.09, 674.77) * mm, "end": v(-1032.09, 661.22) * mm});
            skLineSegment(sketch, "E109", {"start": v(-1032.09, 664.45) * mm, "end": v(-1032.09, 661.22) * mm});
            skPoint(sketch, "E110", {"position": v(-1032.09, 620) * mm});
            skLineSegment(sketch, "E111", {"start": v(-1032.09, 620) * mm, "end": v(-1068.17, 620) * mm});
            skSolve(sketch);
        }
        {
            var Q0;
            {var subQ1=sQuery(id+"F41.wireOp",EDGE,"E107");Q0=makeQuery(id+"F41.imprint","IMPRINT",FACE,{"disambiguationData":[TD([[makeQuery(id+"F41.imprint","IMPRINT",EDGE,{"derivedFrom":subQ1}),1.0]])]});}
            var Q1;
            Q1=sQuery(id+"F36.wireOp",EDGE,"E93");
            revolve(context, id + "F42", {"operationType" : NewBodyOperationType.ADD, "entities" : qUnion([Q0]), "axis" : qUnion([Q1]), "revolveType" : RevolveType.FULL});
        }
        {
            var Q0;
            Q0=makeQuery(id+"F42.opRevolve","SWEPT_FACE",FACE,{"disambiguationData":[OSD([sQuery(id+"F41.wireOp",EDGE,"E109")])]});
            var Q1;
            Q1=sQuery(id+"F41.wireOp",EDGE,"E111");
            var Q2;
            Q2=sQuery(id+"F36.wireOp",EDGE,"E95.filletArc");
            var Q3;
            Q3=sQuery(id+"F36.wireOp",EDGE,"E94");
            var Q4;
            Q4=sQuery(id+"F36.wireOp",EDGE,"E97.filletArc");
            var Q5;
            Q5=sQuery(id+"F36.wireOp",EDGE,"E96");
            var Q6;
            Q6=sQuery(id+"F39.wireOp",EDGE,"E103");
            sweep(context, id + "F43", {"operationType" : NewBodyOperationType.ADD, "profiles" : qUnion([Q0]), "path" : qUnion([Q1, Q2, Q3, Q4, Q5, Q6])});
        }
        {
            var Q0;
            Q0=makeQuery(id+"F43.opSweep","CAP_FACE",FACE,{"disambiguationData":[OSD([sQuery(id+"F39.wireOp",VERTEX,"E100.end"),sQuery(id+"F41.wireOp",EDGE,"E109")])],"isStart":false});
            var sketch = newSketch(context, id + "F44", { "sketchPlane" : qUnion([Q0])});
            skCircle(sketch, "E112", {"center": v(1531.5, 3722) * mm, "radius": 45.25 * mm});
            skCircle(sketch, "E113", {"center": v(1531.5, 3722) * mm, "radius": 80 * mm, "construction": true});
            skCircle(sketch, "E114", {"center": v(1531.5, 3722) * mm, "radius": 100 * mm});
            skCircle(sketch, "E115", {"center": v(1531.5, 3642) * mm, "radius": 9 * mm});
            skCircle(sketch, "E116.1.0", {"center": v(1588.06, 3665.43) * mm, "radius": 9 * mm});
            skCircle(sketch, "E116.2.0", {"center": v(1611.5, 3722) * mm, "radius": 9 * mm});
            skCircle(sketch, "E116.3.0", {"center": v(1588.06, 3778.57) * mm, "radius": 9 * mm});
            skCircle(sketch, "E116.4.0", {"center": v(1531.5, 3802) * mm, "radius": 9 * mm});
            skCircle(sketch, "E116.5.0", {"center": v(1474.93, 3778.57) * mm, "radius": 9 * mm});
            skCircle(sketch, "E116.6.0", {"center": v(1451.5, 3722) * mm, "radius": 9 * mm});
            skCircle(sketch, "E116.7.0", {"center": v(1474.93, 3665.43) * mm, "radius": 9 * mm});
            skCircle(sketch, "E117", {"center": v(1531.5, 3722) * mm, "radius": 44.45 * mm});
            skCircle(sketch, "E118.0", {"center": v(1531.5, 3722) * mm, "radius": 41.22 * mm});
            skSolve(sketch);
        }
        {
            var Q0;
            Q0=qSketchRegion(id+"F44",true);
            var Q1;
            Q1=makeQuery(id+"F44.imprint","IMPRINT",FACE,{"disambiguationData":[TD([[makeQuery(id+"F44.imprint","IMPRINT",EDGE,{"derivedFrom":sQuery(id+"F44.wireOp",EDGE,"E112")}),1.0]])]});
            var Q2;
            Q2=makeQuery(id+"F44.imprint","IMPRINT",FACE,{"disambiguationData":[TD([[makeQuery(id+"F44.imprint","IMPRINT",EDGE,{"derivedFrom":sQuery(id+"F44.wireOp",EDGE,"E117")}),1.0]])]});
            extrude(context, id + "F45", {"entities" : qUnion([Q0, Q1, Q2]), "operationType" : NewBodyOperationType.ADD, "oppositeDirection" : true, "depth" : 20 * mm});
        }
    });
